# Revit family: Haworth_BuzziPicNic_StandardHeight_MeetCollaborativeTable
name_source: partatom
category: Furniture
revit_build: Autodesk Revit 2018 (Build: 20170223_1515(x64)
units: mm (PartAtom-declared; Revit-internal decimal feet)

## family parameters
Always vertical = Yes
Cut with Voids When Loaded = No
OmniClass Number = 23.40.20.00
OmniClass Title = General Furniture and Specialties
Room Calculation Point = No
Shared = No
Work Plane-Based = No

## types (6) — shared parameters
Assembly Code = E2020200
Base Finish = Haworth _ Wood _ Natural Ash BAS-NAT
Custom Size = No
Glide Finish = Haworth _ Polymer _ Black
Manufacturer = Haworth
Model = HCBZ-PNTM-L
Revision = 1
Size = Verify Final Dim. w/ Haworth
Standard Depths = 35.43in, 39.37in, 47.24in
Standard Widths = 62.99in, 70.87in, 78.74in, 86.61in, 94.49in
URL = http://www.haworth.com
URL - Product = https://www.haworth.com
Warranty = http://www.haworth.com
zero-valued in all types: Actual Depth, Actual Height, Actual Width, Depth, Max. Depth, Max. Width, Min. Depth, Min. Width, Width

## per-type parameters (varying)
| type | Description | Laminate Top | Large | Medium | Small | Wood Top |
| HCBZ-PNTM-L - 39.37d 94.49w - Wood Top | Haworth BuzziPicNic Standard Height Meet Collaborative Tables - Wood Top | No | No | Yes | No | Yes |
| HCBZ-PNTM-L - 35.43d 94.49w - Wood Top | Haworth BuzziPicNic Standard Height Meet Collaborative Tables - Wood Top | No | No | No | Yes | Yes |
| HCBZ-PNTM-L - 47.24d 94.49w - Wood Top | Haworth BuzziPicNic Standard Height Meet Collaborative Tables - Wood Top | No | Yes | No | No | Yes |
| HCBZ-PNTM-L - 35.43d 94.49w - Laminate Top | Haworth BuzziPicNic Standard Height Meet Collaborative Tables - Laminate Top | Yes | No | No | Yes | No |
| HCBZ-PNTM-L - 39.37d 94.49w - Laminate Top | Haworth BuzziPicNic Standard Height Meet Collaborative Tables - Laminate Top | Yes | No | Yes | No | No |
| HCBZ-PNTM-L - 47.24d 94.49w - Laminate Top | Haworth BuzziPicNic Standard Height Meet Collaborative Tables - Laminate Top | Yes | Yes | No | No | No |

## geometry (parser evidence)
native form markers: Sweep x3
no freeform markers — native parametric forms only
